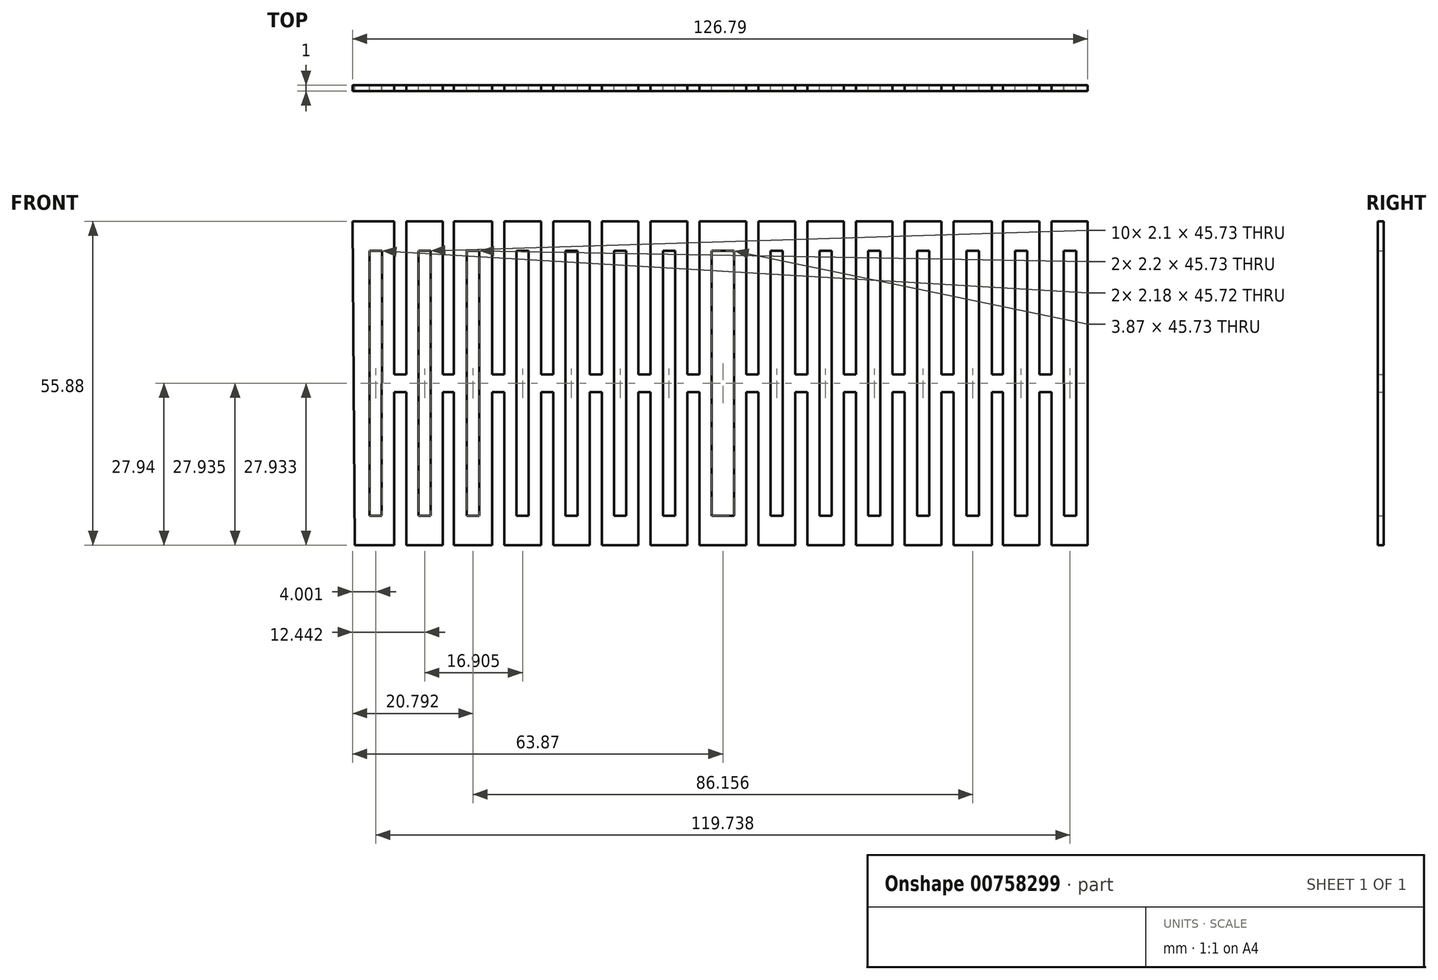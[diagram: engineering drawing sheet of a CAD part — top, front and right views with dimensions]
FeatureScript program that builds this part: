
annotation { "Feature Type Name" : "Feature", "Feature Type Description" : "" }
export const myFeature = defineFeature(function(context is Context, id is Id, definition is map)
    precondition{}
    {
        {
            var Q0;
            Q0=qCreatedBy(makeId("Front.planeOp"),FACE);
            var sketch = newSketch(context, id + "F0", { "sketchPlane" : qUnion([Q0])});
            skLineSegment(sketch, "E0.bottom", {"start": v(-63.87, 27.94) * mm, "end": v(-56.68, 27.94) * mm});
            skLineSegment(sketch, "E0.top", {"start": v(-63.45, -27.94) * mm, "end": v(-56.68, -27.94) * mm});
            skPoint(sketch, "E0.middle", {"position": v(0, 0) * mm});
            skPoint(sketch, "E1.MirrorCS.end.orphan", {"position": v(71.12, 22.86) * mm});
            skPoint(sketch, "E2.MirrorCS.end.orphan", {"position": v(71.12, 17.78) * mm});
            skPoint(sketch, "E2.MirrorCS.start.orphan", {"position": v(66.04, 17.78) * mm});
            skPoint(sketch, "E3.MirrorCS.end.orphan", {"position": v(76.2, 12.7) * mm});
            skPoint(sketch, "E3.MirrorCS.start.orphan", {"position": v(71.12, 12.7) * mm});
            skPoint(sketch, "E4.MirrorCS.start.orphan", {"position": v(76.2, 7.62) * mm});
            skPoint(sketch, "E5.MirrorCS.end.orphan", {"position": v(71.12, 7.62) * mm});
            skPoint(sketch, "E6.MirrorCS.end.orphan", {"position": v(66.04, 9.7) * mm});
            skPoint(sketch, "E6.MirrorCS.start.orphan", {"position": v(71.12, 9.7) * mm});
            skPoint(sketch, "E7.MirrorCS.end.orphan", {"position": v(66.04, 4.62) * mm});
            skPoint(sketch, "E8.MirrorCS.end.orphan", {"position": v(71.12, 4.62) * mm});
            skPoint(sketch, "E9.end.orphan", {"position": v(-71.12, -3.91) * mm});
            skPoint(sketch, "E10.orphan", {"position": v(-71.12, 0) * mm});
            skPoint(sketch, "E11.endSnap0", {"position": v(-71.12, -11.66) * mm});
            skPoint(sketch, "E12.MirrorCS.end.orphan", {"position": v(76.2, -7.62) * mm});
            skPoint(sketch, "E12.MirrorCS.start.orphan", {"position": v(71.12, -7.62) * mm});
            skPoint(sketch, "E13.MirrorCS.end.orphan", {"position": v(76.2, -12.7) * mm});
            skPoint(sketch, "E14.MirrorCS.end.orphan", {"position": v(71.12, -12.7) * mm});
            skPoint(sketch, "E15.MirrorCS.end.orphan", {"position": v(66.04, -17.78) * mm});
            skPoint(sketch, "E15.MirrorCS.start.orphan", {"position": v(71.12, -17.78) * mm});
            skPoint(sketch, "E16.MirrorCS.end.orphan", {"position": v(66.04, -22.86) * mm});
            skPoint(sketch, "E17.MirrorCS.end.orphan", {"position": v(71.12, -22.86) * mm});
            skLineSegment(sketch, "E18", {"start": v(-63.87, 27.94) * mm, "end": v(-60.96, 27.94) * mm});
            skLineSegment(sketch, "E19", {"start": v(-60.96, 22.86) * mm, "end": v(-60.96, -22.86) * mm});
            skLineSegment(sketch, "E20", {"start": v(-60.96, -27.94) * mm, "end": v(-58.86, -27.94) * mm});
            skLineSegment(sketch, "E21", {"start": v(-58.85, -22.86) * mm, "end": v(-58.78, 22.86) * mm});
            skLineSegment(sketch, "E22", {"start": v(-58.77, 27.94) * mm, "end": v(-60.96, 27.94) * mm});
            skLineSegment(sketch, "E23.bottom", {"start": v(-60.96, 27.94) * mm, "end": v(-58.86, 27.94) * mm});
            skLineSegment(sketch, "E23.top", {"start": v(-60.96, 22.86) * mm, "end": v(-58.78, 22.86) * mm});
            skLineSegment(sketch, "E24.bottom", {"start": v(-60.96, -27.94) * mm, "end": v(-58.85, -27.94) * mm});
            skLineSegment(sketch, "E24.top", {"start": v(-60.96, -22.86) * mm, "end": v(-58.85, -22.86) * mm});
            skLineSegment(sketch, "E25", {"start": v(-56.68, 19.28) * mm, "end": v(-56.68, 27.94) * mm});
            skLineSegment(sketch, "E26", {"start": v(-56.68, 27.94) * mm, "end": v(-56.68, 1.5) * mm});
            skLineSegment(sketch, "E27", {"start": v(-54.58, 1.5) * mm, "end": v(-54.58, 27.94) * mm});
            skLineSegment(sketch, "E28", {"start": v(-56.68, -1.5) * mm, "end": v(-56.68, -27.94) * mm});
            skLineSegment(sketch, "E29", {"start": v(-54.58, -1.5) * mm, "end": v(-54.58, -27.94) * mm});
            skLineSegment(sketch, "E30", {"start": v(-54.58, -1.5) * mm, "end": v(-56.68, -1.5) * mm});
            skPoint(sketch, "E30.startSnap0", {"position": v(-71.12, -1.5) * mm});
            skLineSegment(sketch, "E31.MirrorCS", {"start": v(-54.58, 1.5) * mm, "end": v(-56.68, 1.5) * mm});
            skPoint(sketch, "E32.end.orphan", {"position": v(-54.58, 0) * mm});
            skPoint(sketch, "E32.start.orphan", {"position": v(-56.68, 0) * mm});
            skPoint(sketch, "E33.trimOffspring.end.orphan", {"position": v(-71.12, 1.5) * mm});
            skLineSegment(sketch, "E34", {"start": v(-54.58, 27.94) * mm, "end": v(-52.48, 27.94) * mm});
            skLineSegment(sketch, "E35", {"start": v(-52.48, 27.94) * mm, "end": v(-50.38, 27.94) * mm});
            skLineSegment(sketch, "E36", {"start": v(-50.38, 22.86) * mm, "end": v(-50.38, -22.87) * mm});
            skLineSegment(sketch, "E37", {"start": v(-50.38, -27.94) * mm, "end": v(-52.48, -27.94) * mm});
            skLineSegment(sketch, "E38", {"start": v(-52.48, -22.87) * mm, "end": v(-52.48, 22.86) * mm});
            skLineSegment(sketch, "E39.trimOffspring", {"start": v(-52.48, 22.86) * mm, "end": v(-50.38, 22.86) * mm});
            skLineSegment(sketch, "E40.trimOffspring", {"start": v(-52.48, -22.87) * mm, "end": v(-50.38, -22.87) * mm});
            skLineSegment(sketch, "E41", {"start": v(-50.38, 27.94) * mm, "end": v(-48.28, 27.94) * mm});
            skLineSegment(sketch, "E42", {"start": v(-48.28, 27.94) * mm, "end": v(-48.28, 1.5) * mm});
            skLineSegment(sketch, "E43", {"start": v(-46.38, -27.94) * mm, "end": v(-46.38, -1.5) * mm});
            skLineSegment(sketch, "E44", {"start": v(-56.68, 1.5) * mm, "end": v(-54.58, 1.5) * mm});
            skLineSegment(sketch, "E45", {"start": v(-56.68, -1.5) * mm, "end": v(-54.58, -1.5) * mm});
            skLineSegment(sketch, "E46.trimOffspring", {"start": v(-46.38, 1.5) * mm, "end": v(-46.38, 27.94) * mm});
            skLineSegment(sketch, "E47.trimOffspring", {"start": v(-48.28, -1.5) * mm, "end": v(-48.28, -27.94) * mm});
            skLineSegment(sketch, "E48.trimOffspring", {"start": v(-48.28, 1.5) * mm, "end": v(-46.38, 1.5) * mm});
            skLineSegment(sketch, "E49.trimOffspring", {"start": v(-48.28, -1.5) * mm, "end": v(-46.38, -1.5) * mm});
            skLineSegment(sketch, "E50", {"start": v(-46.38, 27.94) * mm, "end": v(-44.18, 27.94) * mm});
            skLineSegment(sketch, "E51", {"start": v(-44.18, 22.86) * mm, "end": v(-44.18, -22.87) * mm});
            skLineSegment(sketch, "E52", {"start": v(-44.18, -27.94) * mm, "end": v(-41.98, -27.94) * mm});
            skLineSegment(sketch, "E53", {"start": v(-41.98, -22.87) * mm, "end": v(-41.98, 22.86) * mm});
            skLineSegment(sketch, "E54", {"start": v(-41.98, 27.94) * mm, "end": v(-44.18, 27.94) * mm});
            skLineSegment(sketch, "E55", {"start": v(-44.18, 22.86) * mm, "end": v(-41.98, 22.86) * mm});
            skLineSegment(sketch, "E56.trimOffspring", {"start": v(-44.18, -22.87) * mm, "end": v(-41.98, -22.87) * mm});
            skPoint(sketch, "E57.end.orphan", {"position": v(-76.2, 12.7) * mm});
            skPoint(sketch, "E58.start.orphan", {"position": v(-76.2, 7.62) * mm});
            skPoint(sketch, "E59.MirrorCS.end.orphan", {"position": v(76.2, 9.7) * mm});
            skPoint(sketch, "E60.orphan", {"position": v(76.2, 4.62) * mm});
            skPoint(sketch, "E61.start.orphan", {"position": v(-66.04, 22.86) * mm});
            skPoint(sketch, "E62.start.orphan", {"position": v(-66.04, 17.78) * mm});
            skPoint(sketch, "E63.start.orphan", {"position": v(-66.04, 9.7) * mm});
            skPoint(sketch, "E64.start.orphan", {"position": v(-66.04, 4.62) * mm});
            skPoint(sketch, "E65.MirrorCS.end.orphan", {"position": v(-71.12, 22.86) * mm});
            skPoint(sketch, "E65.MirrorCS.start.orphan", {"position": v(-76.2, 22.86) * mm});
            skPoint(sketch, "E66.MirrorCS.end.orphan", {"position": v(-71.12, 17.78) * mm});
            skPoint(sketch, "E66.MirrorCS.start.orphan", {"position": v(-76.2, 17.78) * mm});
            skPoint(sketch, "E67.MirrorCS.end.orphan", {"position": v(-66.04, 12.7) * mm});
            skPoint(sketch, "E67.MirrorCS.start.orphan", {"position": v(-71.12, 12.7) * mm});
            skPoint(sketch, "E68.MirrorCS.end.orphan", {"position": v(-71.12, 7.62) * mm});
            skPoint(sketch, "E68.MirrorCS.start.orphan", {"position": v(-66.04, 7.62) * mm});
            skPoint(sketch, "E69.trimOffspring.end.orphan", {"position": v(-71.12, 9.7) * mm});
            skLineSegment(sketch, "E70.MirrorCS", {"start": v(-46.38, -22.87) * mm, "end": v(-46.38, -1.5) * mm});
            skLineSegment(sketch, "E71.trimOffspring", {"start": v(-46.38, 1.5) * mm, "end": v(-46.38, 22.86) * mm});
            skLineSegment(sketch, "E72", {"start": v(-37.7, 27.94) * mm, "end": v(-34.92, 27.94) * mm});
            skPoint(sketch, "E73.MirrorCS.start.orphan", {"position": v(-39.78, 22.86) * mm});
            skPoint(sketch, "E74.start.orphan", {"position": v(-37.68, 1.5) * mm});
            skPoint(sketch, "E75.right.end.orphan", {"position": v(-37.68, 26.36) * mm});
            skPoint(sketch, "E76.start.orphan", {"position": v(-39.78, -22.87) * mm});
            skPoint(sketch, "E77.start.orphan", {"position": v(-76.2, -7.62) * mm});
            skPoint(sketch, "E11.start.orphan", {"position": v(-76.2, -12.7) * mm});
            skPoint(sketch, "E78.start.orphan", {"position": v(-66.04, -17.78) * mm});
            skPoint(sketch, "E79.start.orphan", {"position": v(-66.04, -22.86) * mm});
            skPoint(sketch, "E80.MirrorCS.start.orphan", {"position": v(76.2, 22.86) * mm});
            skPoint(sketch, "E81.MirrorCS.start.orphan", {"position": v(76.2, 17.78) * mm});
            skPoint(sketch, "E82.MirrorCS.end.orphan", {"position": v(66.04, 12.7) * mm});
            skPoint(sketch, "E83.MirrorCS.start.orphan", {"position": v(66.04, 7.62) * mm});
            skPoint(sketch, "E84.MirrorCS.end.orphan", {"position": v(66.04, -7.62) * mm});
            skPoint(sketch, "E85.MirrorCS.end.orphan", {"position": v(66.04, -12.7) * mm});
            skPoint(sketch, "E86.MirrorCS.end.orphan", {"position": v(76.2, -17.78) * mm});
            skPoint(sketch, "E87.MirrorCS.end.orphan", {"position": v(76.2, -22.86) * mm});
            skLineSegment(sketch, "E88", {"start": v(-41.98, 27.94) * mm, "end": v(-39.78, 27.94) * mm});
            skLineSegment(sketch, "E89", {"start": v(-39.78, 27.94) * mm, "end": v(-39.78, 22.86) * mm});
            skLineSegment(sketch, "E90", {"start": v(-39.78, 22.86) * mm, "end": v(-39.78, 1.5) * mm});
            skLineSegment(sketch, "E91", {"start": v(-39.78, 1.5) * mm, "end": v(-37.68, 1.5) * mm});
            skLineSegment(sketch, "E92", {"start": v(-37.68, 1.5) * mm, "end": v(-37.7, 27.94) * mm});
            skLineSegment(sketch, "E93", {"start": v(-39.78, -1.5) * mm, "end": v(-39.78, -27.94) * mm});
            skLineSegment(sketch, "E94", {"start": v(-37.68, -1.5) * mm, "end": v(-37.68, -17.68) * mm});
            skLineSegment(sketch, "E95", {"start": v(-37.68, -17.68) * mm, "end": v(-37.7, -27.94) * mm});
            skLineSegment(sketch, "E96", {"start": v(-39.78, -1.5) * mm, "end": v(-37.68, -1.5) * mm});
            skLineSegment(sketch, "E97", {"start": v(-37.7, 27.94) * mm, "end": v(-31.37, 27.94) * mm});
            skLineSegment(sketch, "E98", {"start": v(-34.92, 27.94) * mm, "end": v(-37.7, 27.94) * mm});
            skLineSegment(sketch, "E99", {"start": v(-35.57, 22.86) * mm, "end": v(-35.57, 17.75) * mm});
            skLineSegment(sketch, "E100", {"start": v(-35.57, 22.86) * mm, "end": v(-33.47, 22.86) * mm});
            skLineSegment(sketch, "E101", {"start": v(-35.57, 17.75) * mm, "end": v(-35.57, -22.87) * mm});
            skLineSegment(sketch, "E102", {"start": v(-35.57, -22.87) * mm, "end": v(-33.47, -22.87) * mm});
            skLineSegment(sketch, "E103", {"start": v(-33.47, -22.87) * mm, "end": v(-33.47, 22.86) * mm});
            skLineSegment(sketch, "E104.MirrorCS", {"start": v(-31.37, 22.86) * mm, "end": v(-31.37, 1.5) * mm});
            skLineSegment(sketch, "E105", {"start": v(-31.37, 22.86) * mm, "end": v(-31.37, 27.94) * mm});
            skLineSegment(sketch, "E106", {"start": v(-29.26, 27.94) * mm, "end": v(-29.26, 1.5) * mm});
            skLineSegment(sketch, "E107", {"start": v(-29.26, 1.5) * mm, "end": v(-31.37, 1.5) * mm});
            skLineSegment(sketch, "E108", {"start": v(-31.37, -1.5) * mm, "end": v(-29.26, -1.5) * mm});
            skLineSegment(sketch, "E109", {"start": v(-29.26, -1.5) * mm, "end": v(-29.26, -27.94) * mm});
            skLineSegment(sketch, "E110", {"start": v(-31.37, -27.94) * mm, "end": v(-31.37, -1.5) * mm});
            skLineSegment(sketch, "E111.MirrorCS", {"start": v(-27.16, 17.75) * mm, "end": v(-27.16, -22.87) * mm});
            skLineSegment(sketch, "E112.MirrorCS", {"start": v(-27.16, 22.86) * mm, "end": v(-27.16, 17.75) * mm});
            skLineSegment(sketch, "E113", {"start": v(-27.16, 22.86) * mm, "end": v(-25.06, 22.86) * mm});
            skLineSegment(sketch, "E114", {"start": v(-25.06, 22.86) * mm, "end": v(-25.06, -22.87) * mm});
            skLineSegment(sketch, "E115", {"start": v(-25.06, -22.87) * mm, "end": v(-27.16, -22.87) * mm});
            skLineSegment(sketch, "E116.MirrorCS", {"start": v(-22.96, 22.86) * mm, "end": v(-22.96, 1.5) * mm});
            skLineSegment(sketch, "E117.MirrorCS", {"start": v(-22.96, 22.86) * mm, "end": v(-22.96, 27.94) * mm});
            skLineSegment(sketch, "E118.MirrorCS", {"start": v(-22.96, -27.94) * mm, "end": v(-22.96, -1.5) * mm});
            skLineSegment(sketch, "E119", {"start": v(-22.96, 1.5) * mm, "end": v(-20.86, 1.5) * mm});
            skLineSegment(sketch, "E120", {"start": v(-20.86, 1.5) * mm, "end": v(-20.86, 27.94) * mm});
            skLineSegment(sketch, "E121", {"start": v(-22.96, -1.5) * mm, "end": v(-20.86, -1.5) * mm});
            skPoint(sketch, "E121.endSnap0", {"position": v(-20.86, 14.72) * mm});
            skLineSegment(sketch, "E122", {"start": v(-20.86, -1.5) * mm, "end": v(-20.86, -27.94) * mm});
            skLineSegment(sketch, "E123.MirrorCS", {"start": v(-18.75, 17.75) * mm, "end": v(-18.75, -22.87) * mm});
            skLineSegment(sketch, "E124.MirrorCS", {"start": v(-18.75, 22.86) * mm, "end": v(-18.75, 17.75) * mm});
            skLineSegment(sketch, "E125", {"start": v(-18.75, 22.86) * mm, "end": v(-16.65, 22.86) * mm});
            skLineSegment(sketch, "E126", {"start": v(-16.65, 22.86) * mm, "end": v(-16.65, -22.87) * mm});
            skLineSegment(sketch, "E127", {"start": v(-16.65, -22.87) * mm, "end": v(-18.75, -22.87) * mm});
            skLineSegment(sketch, "E128.MirrorCS", {"start": v(-14.55, 22.86) * mm, "end": v(-14.55, 1.5) * mm});
            skLineSegment(sketch, "E129.MirrorCS", {"start": v(-14.55, 22.86) * mm, "end": v(-14.55, 27.94) * mm});
            skLineSegment(sketch, "E130.MirrorCS", {"start": v(-14.55, -27.94) * mm, "end": v(-14.55, -1.5) * mm});
            skLineSegment(sketch, "E131", {"start": v(-14.55, 1.5) * mm, "end": v(-12.45, 1.5) * mm});
            skLineSegment(sketch, "E132", {"start": v(-12.45, 1.5) * mm, "end": v(-12.45, 27.94) * mm});
            skLineSegment(sketch, "E133", {"start": v(-14.55, -1.5) * mm, "end": v(-12.45, -1.5) * mm});
            skLineSegment(sketch, "E134", {"start": v(-12.45, -1.5) * mm, "end": v(-12.45, -27.94) * mm});
            skLineSegment(sketch, "E135.MirrorCS", {"start": v(-10.34, 17.75) * mm, "end": v(-10.34, -22.87) * mm});
            skLineSegment(sketch, "E136.MirrorCS", {"start": v(-10.34, 22.86) * mm, "end": v(-10.34, 17.75) * mm});
            skLineSegment(sketch, "E137", {"start": v(-10.34, 22.86) * mm, "end": v(-8.24, 22.86) * mm});
            skLineSegment(sketch, "E138", {"start": v(-8.24, 22.86) * mm, "end": v(-8.24, -22.87) * mm});
            skLineSegment(sketch, "E139", {"start": v(-8.24, -22.87) * mm, "end": v(-10.34, -22.87) * mm});
            skLineSegment(sketch, "E140.MirrorCS", {"start": v(-6.14, 22.86) * mm, "end": v(-6.14, 1.5) * mm});
            skLineSegment(sketch, "E141", {"start": v(-6.14, 22.86) * mm, "end": v(-6.14, 27.94) * mm});
            skLineSegment(sketch, "E142", {"start": v(-6.14, 1.5) * mm, "end": v(-4.04, 1.5) * mm});
            skLineSegment(sketch, "E143", {"start": v(-4.04, 1.5) * mm, "end": v(-4.04, 27.94) * mm});
            skLineSegment(sketch, "E144.MirrorCS", {"start": v(-6.14, -27.94) * mm, "end": v(-6.14, -1.5) * mm});
            skLineSegment(sketch, "E145", {"start": v(-6.14, -1.5) * mm, "end": v(-4.04, -1.5) * mm});
            skLineSegment(sketch, "E146", {"start": v(-4.04, -1.5) * mm, "end": v(-4.04, -27.94) * mm});
            skLineSegment(sketch, "E147.MirrorCS", {"start": v(-1.93, 17.75) * mm, "end": v(-1.93, -22.87) * mm});
            skLineSegment(sketch, "E148.MirrorCS", {"start": v(-1.93, 22.86) * mm, "end": v(-1.93, 17.75) * mm});
            skLineSegment(sketch, "E149", {"start": v(-1.93, 22.86) * mm, "end": v(0, 22.86) * mm});
            skLineSegment(sketch, "E150", {"start": v(0, 22.86) * mm, "end": v(0, -22.87) * mm});
            skLineSegment(sketch, "E151", {"start": v(0, -22.87) * mm, "end": v(-1.93, -22.87) * mm});
            skPoint(sketch, "E152.MirrorCS.start.orphan", {"position": v(-71.12, 27.94) * mm});
            skPoint(sketch, "E153.end.orphan", {"position": v(-71.12, -17.78) * mm});
            skPoint(sketch, "E154.trimOffspring.end.orphan", {"position": v(-71.12, -27.94) * mm});
            skLineSegment(sketch, "E155.MirrorCS", {"start": v(1.93, 22.86) * mm, "end": v(1.93, 17.75) * mm});
            skLineSegment(sketch, "E156.MirrorCS", {"start": v(1.93, 17.75) * mm, "end": v(1.93, -22.87) * mm});
            skLineSegment(sketch, "E157.MirrorCS", {"start": v(1.93, 22.86) * mm, "end": v(0, 22.86) * mm});
            skLineSegment(sketch, "E158.MirrorCS", {"start": v(0, -22.87) * mm, "end": v(1.93, -22.87) * mm});
            skLineSegment(sketch, "E159.MirrorCS", {"start": v(4.04, 1.5) * mm, "end": v(4.04, 27.94) * mm});
            skLineSegment(sketch, "E160.MirrorCS", {"start": v(6.14, 22.86) * mm, "end": v(6.14, 1.5) * mm});
            skLineSegment(sketch, "E161.MirrorCS", {"start": v(6.14, 22.86) * mm, "end": v(6.14, 27.94) * mm});
            skLineSegment(sketch, "E162.MirrorCS", {"start": v(6.14, 1.5) * mm, "end": v(4.04, 1.5) * mm});
            skLineSegment(sketch, "E163.MirrorCS", {"start": v(6.14, -1.5) * mm, "end": v(4.04, -1.5) * mm});
            skLineSegment(sketch, "E164.MirrorCS", {"start": v(6.14, -27.94) * mm, "end": v(6.14, -1.5) * mm});
            skLineSegment(sketch, "E165.MirrorCS", {"start": v(4.04, -1.5) * mm, "end": v(4.04, -27.94) * mm});
            skLineSegment(sketch, "E166.MirrorCS", {"start": v(8.24, 22.86) * mm, "end": v(8.24, -22.87) * mm});
            skLineSegment(sketch, "E167.MirrorCS", {"start": v(10.34, 17.75) * mm, "end": v(10.34, -22.87) * mm});
            skLineSegment(sketch, "E168.MirrorCS", {"start": v(10.34, 22.86) * mm, "end": v(10.34, 17.75) * mm});
            skLineSegment(sketch, "E169.MirrorCS", {"start": v(10.34, 22.86) * mm, "end": v(8.24, 22.86) * mm});
            skLineSegment(sketch, "E170.MirrorCS", {"start": v(8.24, -22.87) * mm, "end": v(10.34, -22.87) * mm});
            skLineSegment(sketch, "E171.MirrorCS", {"start": v(14.55, -1.5) * mm, "end": v(12.45, -1.5) * mm});
            skLineSegment(sketch, "E172.MirrorCS", {"start": v(14.55, -27.94) * mm, "end": v(14.55, -1.5) * mm});
            skLineSegment(sketch, "E173.MirrorCS", {"start": v(12.45, -1.5) * mm, "end": v(12.45, -27.94) * mm});
            skLineSegment(sketch, "E174.MirrorCS", {"start": v(14.55, 22.86) * mm, "end": v(14.55, 1.5) * mm});
            skLineSegment(sketch, "E175.MirrorCS", {"start": v(12.45, 1.5) * mm, "end": v(12.45, 27.94) * mm});
            skLineSegment(sketch, "E176.MirrorCS", {"start": v(14.55, 1.5) * mm, "end": v(12.45, 1.5) * mm});
            skLineSegment(sketch, "E177.MirrorCS", {"start": v(14.55, 22.86) * mm, "end": v(14.55, 27.94) * mm});
            skLineSegment(sketch, "E178.MirrorCS", {"start": v(18.75, 22.86) * mm, "end": v(16.65, 22.86) * mm});
            skLineSegment(sketch, "E179.MirrorCS", {"start": v(16.65, 22.86) * mm, "end": v(16.65, -22.87) * mm});
            skLineSegment(sketch, "E180.MirrorCS", {"start": v(18.75, 22.86) * mm, "end": v(18.75, 17.75) * mm});
            skLineSegment(sketch, "E181.MirrorCS", {"start": v(18.75, 17.75) * mm, "end": v(18.75, -22.87) * mm});
            skLineSegment(sketch, "E182.MirrorCS", {"start": v(16.65, -22.87) * mm, "end": v(18.75, -22.87) * mm});
            skLineSegment(sketch, "E183.MirrorCS", {"start": v(22.96, -27.94) * mm, "end": v(22.96, -1.5) * mm});
            skLineSegment(sketch, "E184.MirrorCS", {"start": v(20.86, -1.5) * mm, "end": v(20.86, -27.94) * mm});
            skLineSegment(sketch, "E185.MirrorCS", {"start": v(22.96, -1.5) * mm, "end": v(20.86, -1.5) * mm});
            skLineSegment(sketch, "E186.MirrorCS", {"start": v(22.96, 1.5) * mm, "end": v(20.86, 1.5) * mm});
            skLineSegment(sketch, "E187.MirrorCS", {"start": v(20.86, 1.5) * mm, "end": v(20.86, 27.94) * mm});
            skLineSegment(sketch, "E188.MirrorCS", {"start": v(22.96, 22.86) * mm, "end": v(22.96, 1.5) * mm});
            skLineSegment(sketch, "E189.MirrorCS", {"start": v(22.96, 22.86) * mm, "end": v(22.96, 27.94) * mm});
            skLineSegment(sketch, "E190.MirrorCS", {"start": v(27.16, 22.86) * mm, "end": v(25.06, 22.86) * mm});
            skLineSegment(sketch, "E191.MirrorCS", {"start": v(27.16, 22.86) * mm, "end": v(27.16, 17.75) * mm});
            skLineSegment(sketch, "E192.MirrorCS", {"start": v(27.16, 17.75) * mm, "end": v(27.16, -22.87) * mm});
            skLineSegment(sketch, "E193.MirrorCS", {"start": v(25.06, 22.86) * mm, "end": v(25.06, -22.87) * mm});
            skLineSegment(sketch, "E194.MirrorCS", {"start": v(25.06, -22.87) * mm, "end": v(27.16, -22.87) * mm});
            skLineSegment(sketch, "E195.MirrorCS", {"start": v(31.37, -1.5) * mm, "end": v(29.26, -1.5) * mm});
            skLineSegment(sketch, "E196.MirrorCS", {"start": v(31.37, -27.94) * mm, "end": v(31.37, -1.5) * mm});
            skLineSegment(sketch, "E197.MirrorCS", {"start": v(29.26, -1.5) * mm, "end": v(29.26, -27.94) * mm});
            skLineSegment(sketch, "E198.MirrorCS", {"start": v(29.26, 1.5) * mm, "end": v(31.37, 1.5) * mm});
            skLineSegment(sketch, "E199.MirrorCS", {"start": v(29.26, 27.94) * mm, "end": v(29.26, 1.5) * mm});
            skLineSegment(sketch, "E200.MirrorCS", {"start": v(31.37, 22.86) * mm, "end": v(31.37, 1.5) * mm});
            skLineSegment(sketch, "E201.MirrorCS", {"start": v(31.37, 22.86) * mm, "end": v(31.37, 27.94) * mm});
            skLineSegment(sketch, "E202.MirrorCS", {"start": v(33.47, -22.87) * mm, "end": v(33.47, 22.86) * mm});
            skLineSegment(sketch, "E203.MirrorCS", {"start": v(35.57, 17.75) * mm, "end": v(35.57, -22.87) * mm});
            skLineSegment(sketch, "E204.MirrorCS", {"start": v(35.57, 22.86) * mm, "end": v(35.57, 17.75) * mm});
            skLineSegment(sketch, "E205.MirrorCS", {"start": v(35.57, 22.86) * mm, "end": v(33.47, 22.86) * mm});
            skLineSegment(sketch, "E206.MirrorCS", {"start": v(35.57, -22.87) * mm, "end": v(33.47, -22.87) * mm});
            skLineSegment(sketch, "E207.MirrorCS", {"start": v(37.68, -1.5) * mm, "end": v(37.68, -17.68) * mm});
            skLineSegment(sketch, "E208.MirrorCS", {"start": v(39.78, -1.5) * mm, "end": v(39.78, -27.94) * mm});
            skLineSegment(sketch, "E209.MirrorCS", {"start": v(37.68, -17.68) * mm, "end": v(37.7, -27.94) * mm});
            skLineSegment(sketch, "E210.MirrorCS", {"start": v(39.78, -1.5) * mm, "end": v(37.68, -1.5) * mm});
            skLineSegment(sketch, "E211.MirrorCS", {"start": v(39.78, 1.5) * mm, "end": v(37.68, 1.5) * mm});
            skLineSegment(sketch, "E212.MirrorCS", {"start": v(39.78, 22.86) * mm, "end": v(39.78, 1.5) * mm});
            skLineSegment(sketch, "E213.MirrorCS", {"start": v(37.68, 1.5) * mm, "end": v(37.7, 27.94) * mm});
            skLineSegment(sketch, "E214.MirrorCS", {"start": v(39.78, 27.94) * mm, "end": v(39.78, 22.86) * mm});
            skLineSegment(sketch, "E215.MirrorCS", {"start": v(44.18, 22.86) * mm, "end": v(41.98, 22.86) * mm});
            skLineSegment(sketch, "E216.MirrorCS", {"start": v(41.98, -22.87) * mm, "end": v(41.98, 22.86) * mm});
            skLineSegment(sketch, "E217.MirrorCS", {"start": v(44.18, 22.86) * mm, "end": v(44.18, -22.87) * mm});
            skLineSegment(sketch, "E218.MirrorCS", {"start": v(44.18, -22.87) * mm, "end": v(41.98, -22.87) * mm});
            skLineSegment(sketch, "E219.MirrorCS", {"start": v(48.28, -1.5) * mm, "end": v(46.38, -1.5) * mm});
            skLineSegment(sketch, "E220.MirrorCS", {"start": v(48.28, -1.5) * mm, "end": v(48.28, -27.94) * mm});
            skLineSegment(sketch, "E221.MirrorCS", {"start": v(46.38, -27.94) * mm, "end": v(46.38, -1.5) * mm});
            skLineSegment(sketch, "E222.MirrorCS", {"start": v(48.28, 1.5) * mm, "end": v(46.38, 1.5) * mm});
            skLineSegment(sketch, "E223.MirrorCS", {"start": v(48.28, 27.94) * mm, "end": v(48.28, 1.5) * mm});
            skLineSegment(sketch, "E224.MirrorCS", {"start": v(46.38, 1.5) * mm, "end": v(46.38, 27.94) * mm});
            skLineSegment(sketch, "E225.MirrorCS", {"start": v(50.38, 22.86) * mm, "end": v(50.38, -22.87) * mm});
            skLineSegment(sketch, "E226.MirrorCS", {"start": v(52.48, -22.87) * mm, "end": v(52.48, 22.86) * mm});
            skLineSegment(sketch, "E227.MirrorCS", {"start": v(52.48, 22.86) * mm, "end": v(50.38, 22.86) * mm});
            skLineSegment(sketch, "E228.MirrorCS", {"start": v(52.48, -22.87) * mm, "end": v(50.38, -22.87) * mm});
            skLineSegment(sketch, "E229.MirrorCS", {"start": v(54.58, 1.5) * mm, "end": v(54.58, 27.94) * mm});
            skLineSegment(sketch, "E230.MirrorCS", {"start": v(56.68, 27.94) * mm, "end": v(56.68, 1.5) * mm});
            skLineSegment(sketch, "E231.MirrorCS", {"start": v(54.58, 1.5) * mm, "end": v(56.68, 1.5) * mm});
            skLineSegment(sketch, "E232.MirrorCS", {"start": v(56.68, -1.5) * mm, "end": v(54.58, -1.5) * mm});
            skLineSegment(sketch, "E233.MirrorCS", {"start": v(56.68, -1.5) * mm, "end": v(56.68, -27.94) * mm});
            skLineSegment(sketch, "E234.MirrorCS", {"start": v(54.58, -1.5) * mm, "end": v(54.58, -27.94) * mm});
            skLineSegment(sketch, "E235.MirrorCS", {"start": v(60.96, 22.86) * mm, "end": v(60.96, -22.86) * mm});
            skLineSegment(sketch, "E236.MirrorCS", {"start": v(58.85, -22.86) * mm, "end": v(58.78, 22.86) * mm});
            skLineSegment(sketch, "E237.MirrorCS", {"start": v(60.96, 22.86) * mm, "end": v(58.78, 22.86) * mm});
            skLineSegment(sketch, "E238.MirrorCS", {"start": v(60.96, -22.86) * mm, "end": v(58.85, -22.86) * mm});
            skLineSegment(sketch, "E239", {"start": v(-60.96, 27.94) * mm, "end": v(-63.87, 27.94) * mm});
            skLineSegment(sketch, "E240", {"start": v(-63.45, -27.94) * mm, "end": v(-60.96, -27.94) * mm});
            skLineSegment(sketch, "E241", {"start": v(-63.87, 27.94) * mm, "end": v(-63.45, -27.94) * mm});
            skPoint(sketch, "E242.trimOffspring.start.orphan", {"position": v(-71.12, -22.86) * mm});
            skPoint(sketch, "E243.orphan", {"position": v(-71.12, 4.62) * mm});
            skPoint(sketch, "E244.trimOffspring.end.orphan", {"position": v(-71.12, -7.62) * mm});
            skPoint(sketch, "E245.trimOffspring.start.orphan", {"position": v(-71.12, -12.7) * mm});
            skLineSegment(sketch, "E246", {"start": v(62.92, 27.94) * mm, "end": v(62.92, -27.94) * mm});
            skPoint(sketch, "E247.start.orphan", {"position": v(71.12, 27.94) * mm});
            skPoint(sketch, "E248.trimOffspring.end.orphan", {"position": v(71.12, -27.94) * mm});
            skLineSegment(sketch, "E249.trimOffspring", {"start": v(56.68, -27.94) * mm, "end": v(62.92, -27.94) * mm});
            skLineSegment(sketch, "E250.trimOffspring", {"start": v(56.68, 27.94) * mm, "end": v(62.92, 27.94) * mm});
            skLineSegment(sketch, "E251.trimOffspring", {"start": v(48.28, 27.94) * mm, "end": v(54.58, 27.94) * mm});
            skLineSegment(sketch, "E252.trimOffspring", {"start": v(48.28, -27.94) * mm, "end": v(54.58, -27.94) * mm});
            skLineSegment(sketch, "E253.trimOffspring", {"start": v(39.78, -27.94) * mm, "end": v(46.38, -27.94) * mm});
            skLineSegment(sketch, "E254.trimOffspring", {"start": v(31.37, -27.94) * mm, "end": v(37.7, -27.94) * mm});
            skLineSegment(sketch, "E255.trimOffspring", {"start": v(22.96, -27.94) * mm, "end": v(29.26, -27.94) * mm});
            skLineSegment(sketch, "E256.trimOffspring", {"start": v(14.55, -27.94) * mm, "end": v(20.86, -27.94) * mm});
            skLineSegment(sketch, "E257.trimOffspring", {"start": v(39.78, 27.94) * mm, "end": v(46.38, 27.94) * mm});
            skLineSegment(sketch, "E258.trimOffspring", {"start": v(31.37, 27.94) * mm, "end": v(37.7, 27.94) * mm});
            skLineSegment(sketch, "E259.trimOffspring", {"start": v(22.96, 27.94) * mm, "end": v(29.26, 27.94) * mm});
            skLineSegment(sketch, "E260.trimOffspring", {"start": v(14.55, 27.94) * mm, "end": v(20.86, 27.94) * mm});
            skLineSegment(sketch, "E261.trimOffspring", {"start": v(6.14, 27.94) * mm, "end": v(12.45, 27.94) * mm});
            skLineSegment(sketch, "E262.trimOffspring", {"start": v(-4.04, 27.94) * mm, "end": v(4.04, 27.94) * mm});
            skLineSegment(sketch, "E263.trimOffspring", {"start": v(6.14, -27.94) * mm, "end": v(12.45, -27.94) * mm});
            skLineSegment(sketch, "E264.trimOffspring", {"start": v(-4.04, -27.94) * mm, "end": v(4.04, -27.94) * mm});
            skLineSegment(sketch, "E265.trimOffspring", {"start": v(-12.45, -27.94) * mm, "end": v(-6.14, -27.94) * mm});
            skLineSegment(sketch, "E266.trimOffspring", {"start": v(-20.86, -27.94) * mm, "end": v(-14.55, -27.94) * mm});
            skLineSegment(sketch, "E267.trimOffspring", {"start": v(-29.26, -27.94) * mm, "end": v(-22.96, -27.94) * mm});
            skLineSegment(sketch, "E268.trimOffspring", {"start": v(-37.7, -27.94) * mm, "end": v(-31.37, -27.94) * mm});
            skLineSegment(sketch, "E269.trimOffspring", {"start": v(-46.38, -27.94) * mm, "end": v(-39.78, -27.94) * mm});
            skLineSegment(sketch, "E270.trimOffspring", {"start": v(-54.58, -27.94) * mm, "end": v(-48.28, -27.94) * mm});
            skLineSegment(sketch, "E271.trimOffspring", {"start": v(-54.58, 27.94) * mm, "end": v(-48.28, 27.94) * mm});
            skLineSegment(sketch, "E272.trimOffspring", {"start": v(-46.38, 27.94) * mm, "end": v(-41.98, 27.94) * mm});
            skLineSegment(sketch, "E273.trimOffspring", {"start": v(-29.26, 27.94) * mm, "end": v(-22.96, 27.94) * mm});
            skPoint(sketch, "E274.end.orphan", {"position": v(-30.83, 27.94) * mm});
            skLineSegment(sketch, "E275.trimOffspring", {"start": v(-20.86, 27.94) * mm, "end": v(-14.55, 27.94) * mm});
            skLineSegment(sketch, "E276.trimOffspring", {"start": v(-12.45, 27.94) * mm, "end": v(-6.14, 27.94) * mm});
            skSolve(sketch);
        }
        {
            var Q0;
            Q0 = qSketchRegion(id + "F0", true);
            extrude(context, id + "F1", {"entities" : qUnion([Q0]), "depth" : 1 * mm, "offsetDistance" : 25.4 * mm});
        }
    });
